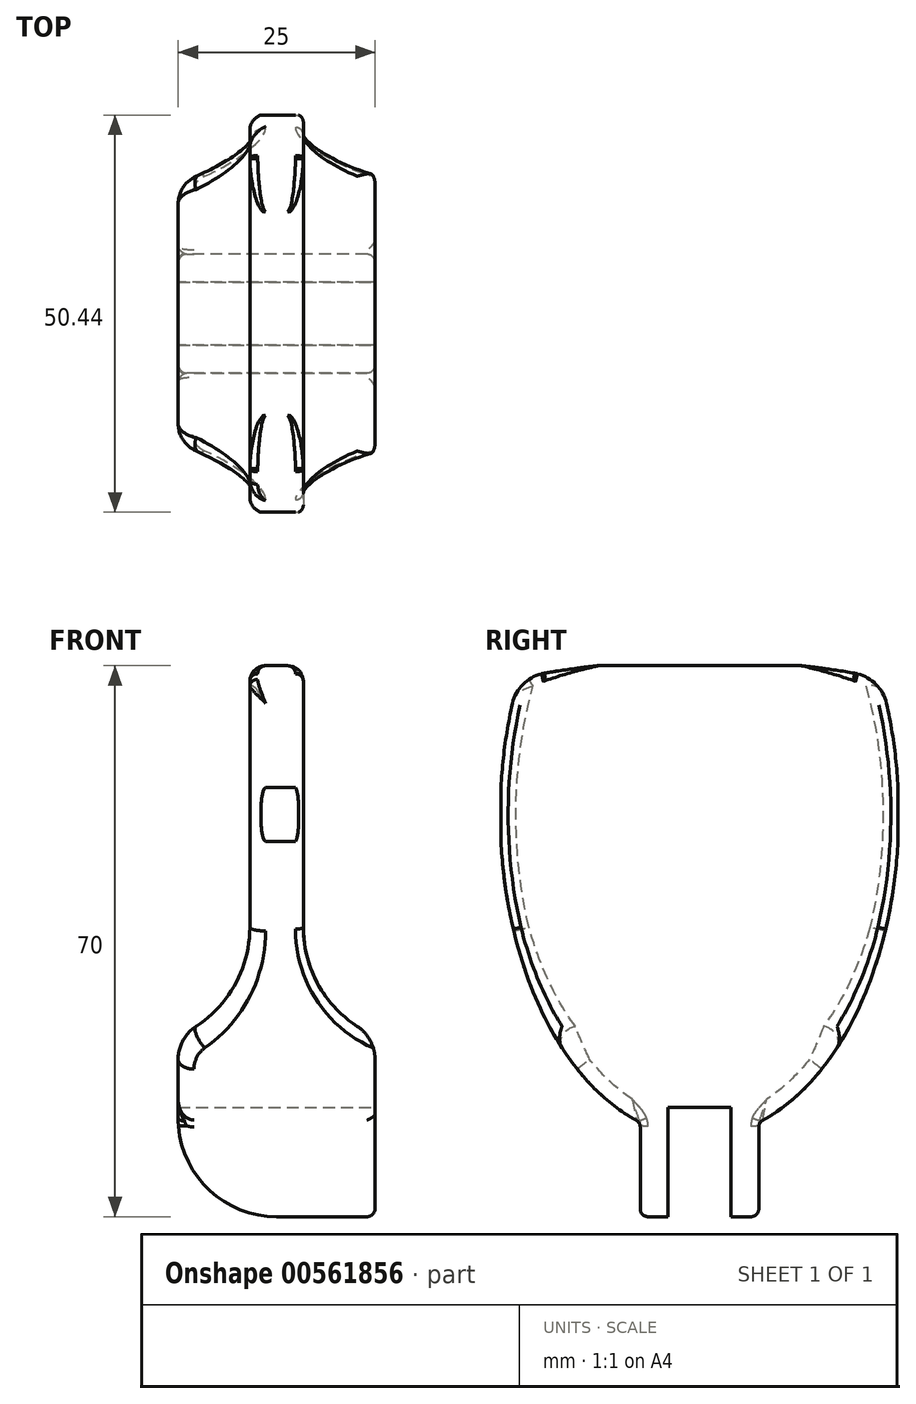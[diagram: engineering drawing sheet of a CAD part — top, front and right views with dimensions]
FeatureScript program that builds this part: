
annotation { "Feature Type Name" : "Feature", "Feature Type Description" : "" }
export const myFeature = defineFeature(function(context is Context, id is Id, definition is map)
    precondition{}
    {
        {
            var Q0;
            Q0=qCreatedBy(makeId("Front.planeOp"),FACE);
            var sketch = newSketch(context, id + "F0", { "sketchPlane" : qUnion([Q0])});
            skArc(sketch, "E0", {"start": v(-12.5, -14.27) * mm, "mid": v(-8.84, -23.11) * mm, "end": v(0, -26.77) * mm});
            skLineSegment(sketch, "E1.top", {"start": v(1.4, 43.23) * mm, "end": v(-1.4, 43.23) * mm});
            skLineSegment(sketch, "E1.left", {"start": v(3.4, 10) * mm, "end": v(3.4, 41.23) * mm});
            skLineSegment(sketch, "E1.right", {"start": v(-3.4, 10) * mm, "end": v(-3.4, 41.23) * mm});
            skPoint(sketch, "E1.middle", {"position": v(0, 20.49) * mm});
            skLineSegment(sketch, "E2.bottom", {"start": v(-7.5, -1.77) * mm, "end": v(7.5, -1.77) * mm});
            skLineSegment(sketch, "E2.top", {"start": v(0, -26.77) * mm, "end": v(11.5, -26.77) * mm});
            skLineSegment(sketch, "E2.left", {"start": v(-12.5, -6.77) * mm, "end": v(-12.5, -14.27) * mm});
            skLineSegment(sketch, "E2.right", {"start": v(12.5, -6.77) * mm, "end": v(12.5, -25.77) * mm});
            skArc(sketch, "E3", {"start": v(-7.5, -1.77) * mm, "mid": v(-11.04, -3.24) * mm, "end": v(-12.5, -6.77) * mm});
            skArc(sketch, "E4", {"start": v(12.5, -6.77) * mm, "mid": v(11.04, -3.24) * mm, "end": v(7.5, -1.77) * mm});
            skArc(sketch, "E5", {"start": v(-10.22, -2.58) * mm, "mid": v(-5.22, 2.84) * mm, "end": v(-3.4, 10) * mm});
            skArc(sketch, "E6", {"start": v(3.4, 10) * mm, "mid": v(5.22, 2.84) * mm, "end": v(10.22, -2.58) * mm});
            skPoint(sketch, "E7.orphan", {"position": v(-3.4, -2.25) * mm});
            skPoint(sketch, "E8.trimOffspring.end.orphan", {"position": v(3.4, -2.25) * mm});
            skArc(sketch, "E9", {"start": v(11.5, -26.77) * mm, "mid": v(12.2, -26.48) * mm, "end": v(12.5, -25.77) * mm});
            skPoint(sketch, "E10.visualSharp", {"position": v(-3.4, 43.23) * mm});
            skArc(sketch, "E10.filletArc", {"start": v(-1.4, 43.23) * mm, "mid": v(-2.81, 42.64) * mm, "end": v(-3.4, 41.23) * mm});
            skPoint(sketch, "E11.visualSharp", {"position": v(3.4, 43.23) * mm});
            skArc(sketch, "E11.filletArc", {"start": v(3.4, 41.23) * mm, "mid": v(2.81, 42.64) * mm, "end": v(1.4, 43.23) * mm});
            skSolve(sketch);
        }
        {
            var Q0;
            Q0=makeQuery(id+"F0.imprint","IMPRINT",FACE,{"disambiguationData":[TD([[makeQuery(id+"F0.imprint","IMPRINT",EDGE,{"derivedFrom":sQuery(id+"F0.wireOp",EDGE,"E1.top")}),1.0]])]});
            var Q1;
            Q1=makeQuery(id+"F0.imprint","IMPRINT",FACE,{"disambiguationData":[TD([[makeQuery(id+"F0.imprint","IMPRINT",EDGE,{"derivedFrom":sQuery(id+"F0.wireOp",EDGE,"E0")}),1.0]])]});
            extrude(context, id + "F1", {"entities" : qUnion([Q0, Q1]), "endBound" : BoundingType.SYMMETRIC, "depth" : 50.43 * mm, "offsetDistance" : 25 * mm});
        }
        {
            var Q0;
            Q0=makeQuery(id+"F1.opExtrude","SWEPT_FACE",FACE,{"disambiguationData":[OSD([sQuery(id+"F0.wireOp",EDGE,"E2.right")])]});
            cPlane(context, id + "F2", {"entities" : qUnion([Q0]), "cplaneType" : CPlaneType.OFFSET, "offset" : 0 * mm, "width" : 150 * mm, "height" : 150 * mm});
        }
        {
            var Q0;
            Q0=qCreatedBy(id+"F2.planeOp",FACE);
            var sketch = newSketch(context, id + "F3", { "sketchPlane" : qUnion([Q0])});
            skLineSegment(sketch, "E12.bottom", {"start": v(-26.66, 43.94) * mm, "end": v(27.44, 43.94) * mm});
            skLineSegment(sketch, "E12.top", {"start": v(-26.66, -27.37) * mm, "end": v(27.44, -27.37) * mm});
            skLineSegment(sketch, "E12.left", {"start": v(-26.66, 43.94) * mm, "end": v(-26.66, -27.37) * mm});
            skLineSegment(sketch, "E12.right", {"start": v(27.44, 43.94) * mm, "end": v(27.44, -27.37) * mm});
            skLineSegment(sketch, "E13.bottom", {"start": v(4, -26.88) * mm, "end": v(-4, -26.88) * mm});
            skLineSegment(sketch, "E13.top", {"start": v(4, -12.88) * mm, "end": v(-4, -12.88) * mm});
            skLineSegment(sketch, "E13.left", {"start": v(4, -26.88) * mm, "end": v(4, -12.88) * mm});
            skLineSegment(sketch, "E13.right", {"start": v(-4, -26.88) * mm, "end": v(-4, -12.88) * mm});
            skPoint(sketch, "E13.middle", {"position": v(0, -19.88) * mm});
            skLineSegment(sketch, "E14.top", {"start": v(7.5, -26.88) * mm, "end": v(-7.5, -26.88) * mm});
            skPoint(sketch, "E14.middle", {"position": v(0, -18.2) * mm});
            skLineSegment(sketch, "E15.bottom", {"start": v(7.53, -26.88) * mm, "end": v(27.44, -26.88) * mm});
            skLineSegment(sketch, "E15.top", {"start": v(7.53, -12.88) * mm, "end": v(27.44, -12.88) * mm});
            skLineSegment(sketch, "E15.left", {"start": v(7.53, -26.88) * mm, "end": v(7.53, -12.88) * mm});
            skLineSegment(sketch, "E15.right", {"start": v(27.44, -26.88) * mm, "end": v(27.44, -12.88) * mm});
            skLineSegment(sketch, "E16.bottom", {"start": v(-7.53, -26.88) * mm, "end": v(-26.66, -26.88) * mm});
            skLineSegment(sketch, "E16.top", {"start": v(-7.53, -12.88) * mm, "end": v(-26.66, -12.88) * mm});
            skLineSegment(sketch, "E16.left", {"start": v(-7.53, -26.88) * mm, "end": v(-7.53, -12.88) * mm});
            skLineSegment(sketch, "E16.right", {"start": v(-26.66, -26.88) * mm, "end": v(-26.66, -12.88) * mm});
            skArc(sketch, "E17", {"start": v(19.71, 42.27) * mm, "mid": v(0, 43.94) * mm, "end": v(-19.71, 42.27) * mm});
            skArc(sketch, "E18", {"start": v(-17.38, 13.5) * mm, "mid": v(0, -0.88) * mm, "end": v(17.38, 13.5) * mm});
            skEllipticalArc(sketch, "E19", {});
            skFitSpline(sketch, "E20.0", {"points": [v(1.4, 58.28) * mm, v(0, 58.39) * mm, v(-1.4, 58.28) * mm, v(-2.82, 57.94) * mm, v(-4.3, 57.34) * mm, v(-5.83, 56.46) * mm, v(-7.4, 55.26) * mm, v(-8.97, 53.74) * mm, v(-10.27, 52.2) * mm, v(-11.28, 50.79) * mm, v(-12.02, 49.65) * mm, v(-12.73, 48.43) * mm, v(-13.64, 46.73) * mm, v(-14.7, 44.44) * mm, v(-15.8, 41.46) * mm, v(-16.72, 38.3) * mm, v(-17.45, 34.97) * mm, v(-18, 31.5) * mm, v(-18.27, 28.54) * mm, v(-18.38, 26.14) * mm, v(-18.4, 24.31) * mm, v(-18.38, 22.5) * mm, v(-18.27, 20.09) * mm, v(-18, 17.12) * mm, v(-17.45, 13.66) * mm, v(-16.72, 10.33) * mm, v(-15.8, 7.16) * mm, v(-14.7, 4.2) * mm, v(-13.64, 1.9) * mm, v(-12.73, 0.2) * mm, v(-12.02, -1.02) * mm, v(-11.28, -2.16) * mm, v(-10.27, -3.57) * mm, v(-8.97, -5.11) * mm, v(-7.4, -6.64) * mm, v(-5.83, -7.83) * mm, v(-4.3, -8.71) * mm, v(-2.82, -9.3) * mm, v(-1.4, -9.65) * mm, v(0, -9.76) * mm, v(1.4, -9.65) * mm, v(2.82, -9.3) * mm, v(4.3, -8.71) * mm, v(5.83, -7.83) * mm, v(7.4, -6.64) * mm, v(8.97, -5.11) * mm, v(10.27, -3.57) * mm, v(11.28, -2.16) * mm, v(12.02, -1.02) * mm, v(12.73, 0.2) * mm, v(13.64, 1.9) * mm, v(14.7, 4.2) * mm, v(15.8, 7.16) * mm, v(16.72, 10.33) * mm, v(17.45, 13.66) * mm, v(18, 17.12) * mm, v(18.27, 20.09) * mm, v(18.38, 22.5) * mm, v(18.4, 24.31) * mm, v(18.38, 26.14) * mm, v(18.27, 28.54) * mm, v(18, 31.5) * mm, v(17.45, 34.97) * mm, v(16.72, 38.3) * mm, v(15.8, 41.46) * mm, v(14.7, 44.44) * mm, v(13.64, 46.73) * mm, v(12.73, 48.43) * mm, v(12.02, 49.65) * mm, v(11.28, 50.79) * mm, v(10.27, 52.2) * mm, v(8.97, 53.74) * mm, v(7.4, 55.26) * mm, v(5.83, 56.46) * mm, v(4.3, 57.34) * mm, v(2.82, 57.94) * mm, v(1.4, 58.28) * mm, v(0, 58.39) * mm, v(-1.4, 58.28) * mm]});
            skFitSpline(sketch, "E21.trimOffspring", {"points": [v(1.4, 58.28) * mm, v(0, 58.39) * mm, v(-1.4, 58.28) * mm, v(-2.82, 57.94) * mm, v(-4.3, 57.34) * mm, v(-5.83, 56.46) * mm, v(-7.4, 55.26) * mm, v(-8.97, 53.74) * mm, v(-10.27, 52.2) * mm, v(-11.28, 50.79) * mm, v(-12.02, 49.65) * mm, v(-12.73, 48.43) * mm, v(-13.64, 46.73) * mm, v(-14.7, 44.44) * mm, v(-15.8, 41.46) * mm, v(-16.72, 38.3) * mm, v(-17.45, 34.97) * mm, v(-18, 31.5) * mm, v(-18.27, 28.54) * mm, v(-18.38, 26.14) * mm, v(-18.4, 24.31) * mm, v(-18.38, 22.5) * mm, v(-18.27, 20.09) * mm, v(-18, 17.12) * mm, v(-17.45, 13.66) * mm, v(-16.72, 10.33) * mm, v(-15.8, 7.16) * mm, v(-14.7, 4.2) * mm, v(-13.64, 1.9) * mm, v(-12.73, 0.2) * mm, v(-12.02, -1.02) * mm, v(-11.28, -2.16) * mm, v(-10.27, -3.57) * mm, v(-8.97, -5.11) * mm, v(-7.4, -6.64) * mm, v(-5.83, -7.83) * mm, v(-4.3, -8.71) * mm, v(-2.82, -9.3) * mm, v(-1.4, -9.65) * mm, v(0, -9.76) * mm, v(1.4, -9.65) * mm, v(2.82, -9.3) * mm, v(4.3, -8.71) * mm, v(5.83, -7.83) * mm, v(7.4, -6.64) * mm, v(8.97, -5.11) * mm, v(10.27, -3.57) * mm, v(11.28, -2.16) * mm, v(12.02, -1.02) * mm, v(12.73, 0.2) * mm, v(13.64, 1.9) * mm, v(14.7, 4.2) * mm, v(15.8, 7.16) * mm, v(16.72, 10.33) * mm, v(17.45, 13.66) * mm, v(18, 17.12) * mm, v(18.27, 20.09) * mm, v(18.38, 22.5) * mm, v(18.4, 24.31) * mm, v(18.38, 26.14) * mm, v(18.27, 28.54) * mm, v(18, 31.5) * mm, v(17.45, 34.97) * mm, v(16.72, 38.3) * mm, v(15.8, 41.46) * mm, v(14.7, 44.44) * mm, v(13.64, 46.73) * mm, v(12.73, 48.43) * mm, v(12.02, 49.65) * mm, v(11.28, 50.79) * mm, v(10.27, 52.2) * mm, v(8.97, 53.74) * mm, v(7.4, 55.26) * mm, v(5.83, 56.46) * mm, v(4.3, 57.34) * mm, v(2.82, 57.94) * mm, v(1.4, 58.28) * mm, v(0, 58.39) * mm, v(-1.4, 58.28) * mm]});
            skEllipticalArc(sketch, "E22.trimOffspring", {});
            skArc(sketch, "E23.trimOffspring", {"start": v(17.28, 35.67) * mm, "mid": v(0, 37.03) * mm, "end": v(-17.28, 35.67) * mm});
            skPoint(sketch, "E24.visualSharp", {"position": v(-22.92, 41.68) * mm});
            skArc(sketch, "E24.filletArc", {"start": v(-19.71, 42.27) * mm, "mid": v(-22.31, 40.97) * mm, "end": v(-23.75, 38.45) * mm});
            skPoint(sketch, "E25.visualSharp", {"position": v(22.92, 41.68) * mm});
            skArc(sketch, "E25.filletArc", {"start": v(23.75, 38.45) * mm, "mid": v(22.31, 40.97) * mm, "end": v(19.71, 42.27) * mm});
            const initialGuessF3  = {"E19": [0, 0.02431378650389769, 0, 1, 0.040948620362707154, 0.02530453173425501, 1.218304167247893, 2.83944091341062], "E22.trimOffspring": [-3.4531458895558287e-09, 0.02431372548767801, -5.071851758616154e-07, 1, 0.04095312103342927, 0.02530426842214503, 3.443746959321061, 5.0648344110688175]};
            skSetInitialGuess(sketch, initialGuessF3);
            skSolve(sketch);
        }
        {
            var Q0;
            Q0=makeQuery(id+"F3.imprint","IMPRINT",FACE,{"disambiguationData":[TD([[makeQuery(id+"F3.imprint","IMPRINT",EDGE,{"derivedFrom":sQuery(id+"F3.wireOp",EDGE,"E13.top")}),1.0]])]});
            var Q1;
            Q1=makeQuery(id+"F3.imprint","IMPRINT",FACE,{"disambiguationData":[TD([[makeQuery(id+"F3.imprint","IMPRINT",EDGE,{"derivedFrom":sQuery(id+"F3.wireOp",EDGE,"E16.bottom")}),-1.0]])]});
            var Q2;
            Q2=makeQuery(id+"F3.imprint","IMPRINT",FACE,{"disambiguationData":[TD([[makeQuery(id+"F3.imprint","IMPRINT",EDGE,{"derivedFrom":sQuery(id+"F3.wireOp",EDGE,"E15.bottom")}),1.0]])]});
            var Q3;
            Q3=makeQuery(id+"F3.imprint","IMPRINT",FACE,{"disambiguationData":[TD([[makeQuery(id+"F3.imprint","IMPRINT",EDGE,{"derivedFrom":sQuery(id+"F3.wireOp",EDGE,"E18")}),1.0]])]});
            var Q4;
            {var subQ0=sQuery(id+"F3.wireOp",EDGE,"E25.filletArc");Q4=makeQuery(id+"F3.imprint","IMPRINT",FACE,{"disambiguationData":[TD([[makeQuery(id+"F3.imprint","IMPRINT",EDGE,{"derivedFrom":subQ0}),-1.0]])]});}
            var Q5;
            {var subQ0=sQuery(id+"F3.wireOp",EDGE,"E24.filletArc");Q5=makeQuery(id+"F3.imprint","IMPRINT",FACE,{"disambiguationData":[TD([[makeQuery(id+"F3.imprint","IMPRINT",EDGE,{"derivedFrom":subQ0}),-1.0]])]});}
            extrude(context, id + "F4", {"entities" : qUnion([Q0, Q1, Q2, Q3, Q4, Q5]), "operationType" : NewBodyOperationType.REMOVE, "oppositeDirection" : true, "depth" : 25 * mm, "offsetDistance" : 25 * mm});
        }
        {
            var Q0;
            Q0=makeQuery(id+"F4.boolean.opBoolean","INTERSECT",EDGE,{"derivedFrom":[makeQuery(id+"F1.opExtrude","SWEPT_FACE",FACE,{"disambiguationData":[OSD([sQuery(id+"F0.wireOp",EDGE,"E6")])]}),makeQuery(id+"F4.opExtrude","SWEPT_FACE",FACE,{"disambiguationData":[OSD([sQuery(id+"F3.wireOp",EDGE,"E18")])]})]});
            var Q1;
            Q1=makeQuery(id+"F4.boolean.opBoolean","INTERSECT",EDGE,{"derivedFrom":[makeQuery(id+"F1.opExtrude","SWEPT_FACE",FACE,{"disambiguationData":[OSD([sQuery(id+"F0.wireOp",EDGE,"E1.left")])]}),makeQuery(id+"F4.opExtrude","SWEPT_FACE",FACE,{"disambiguationData":[OSD([sQuery(id+"F3.wireOp",EDGE,"E20.0")])]})]});
            var Q2;
            Q2=makeQuery(id+"F4.boolean.opBoolean","INTERSECT",EDGE,{"derivedFrom":[makeQuery(id+"F1.opExtrude","SWEPT_FACE",FACE,{"disambiguationData":[OSD([sQuery(id+"F0.wireOp",EDGE,"E1.left")])]}),makeQuery(id+"F4.opExtrude","SWEPT_FACE",FACE,{"disambiguationData":[OSD([sQuery(id+"F3.wireOp",EDGE,"E23.trimOffspring")])]})]});
            var Q3;
            Q3=makeQuery(id+"F4.boolean.opBoolean","INTERSECT",EDGE,{"derivedFrom":[makeQuery(id+"F1.opExtrude","SWEPT_FACE",FACE,{"disambiguationData":[OSD([sQuery(id+"F0.wireOp",EDGE,"E1.left")])]}),makeQuery(id+"F4.opExtrude","SWEPT_FACE",FACE,{"disambiguationData":[OSD([sQuery(id+"F3.wireOp",EDGE,"E21.trimOffspring")])]})]});
            var Q4;
            Q4=makeQuery(id+"F4.boolean.opBoolean","INTERSECT",EDGE,{"derivedFrom":[makeQuery(id+"F1.opExtrude","SWEPT_FACE",FACE,{"disambiguationData":[OSD([sQuery(id+"F0.wireOp",EDGE,"E5")])]}),makeQuery(id+"F4.opExtrude","SWEPT_FACE",FACE,{"disambiguationData":[OSD([sQuery(id+"F3.wireOp",EDGE,"E19")])]})]});
            var Q5;
            Q5=makeQuery(id+"F4.boolean.opBoolean","INTERSECT",EDGE,{"derivedFrom":[makeQuery(id+"F1.opExtrude","SWEPT_FACE",FACE,{"disambiguationData":[OSD([sQuery(id+"F0.wireOp",EDGE,"E5")])]}),makeQuery(id+"F4.opExtrude","SWEPT_FACE",FACE,{"disambiguationData":[OSD([sQuery(id+"F3.wireOp",EDGE,"E22.trimOffspring")])]})]});
            var Q6;
            Q6=makeQuery(id+"F4.boolean.opBoolean","COPY",EDGE,{"derivedFrom":makeQuery(id+"F4.opExtrude","CAP_EDGE",EDGE,{"disambiguationData":[OSD([sQuery(id+"F3.wireOp",EDGE,"E22.trimOffspring")])],"isStart":true})});
            var Q7;
            Q7=makeQuery(id+"F4.boolean.opBoolean","COPY",EDGE,{"derivedFrom":makeQuery(id+"F4.opExtrude","CAP_EDGE",EDGE,{"disambiguationData":[OSD([sQuery(id+"F3.wireOp",EDGE,"E19")])],"isStart":true})});
            var Q8;
            Q8=makeQuery(id+"F4.boolean.opBoolean","INTERSECT",EDGE,{"derivedFrom":[makeQuery(id+"F1.opExtrude","SWEPT_FACE",FACE,{"disambiguationData":[OSD([sQuery(id+"F0.wireOp",EDGE,"E5")])]}),makeQuery(id+"F4.opExtrude","SWEPT_FACE",FACE,{"disambiguationData":[OSD([sQuery(id+"F3.wireOp",EDGE,"E18")])]})]});
            var Q9;
            Q9=makeQuery(id+"F4.boolean.opBoolean","INTERSECT",EDGE,{"derivedFrom":[makeQuery(id+"F1.opExtrude","SWEPT_FACE",FACE,{"disambiguationData":[OSD([sQuery(id+"F0.wireOp",EDGE,"E1.right")])]}),makeQuery(id+"F4.opExtrude","SWEPT_FACE",FACE,{"disambiguationData":[OSD([sQuery(id+"F3.wireOp",EDGE,"E20.0")])]})]});
            var Q10;
            Q10=makeQuery(id+"F4.boolean.opBoolean","INTERSECT",EDGE,{"derivedFrom":[makeQuery(id+"F1.opExtrude","SWEPT_FACE",FACE,{"disambiguationData":[OSD([sQuery(id+"F0.wireOp",EDGE,"E1.right")])]}),makeQuery(id+"F4.opExtrude","SWEPT_FACE",FACE,{"disambiguationData":[OSD([sQuery(id+"F3.wireOp",EDGE,"E23.trimOffspring")])]})]});
            var Q11;
            Q11=makeQuery(id+"F4.boolean.opBoolean","INTERSECT",EDGE,{"derivedFrom":[makeQuery(id+"F1.opExtrude","SWEPT_FACE",FACE,{"disambiguationData":[OSD([sQuery(id+"F0.wireOp",EDGE,"E1.right")])]}),makeQuery(id+"F4.opExtrude","SWEPT_FACE",FACE,{"disambiguationData":[OSD([sQuery(id+"F3.wireOp",EDGE,"E21.trimOffspring")])]})]});
            fillet(context, id + "F5", {"entities" : qUnion([Q0, Q1, Q2, Q3, Q4, Q5, Q6, Q7, Q8, Q9, Q10, Q11]), "radius" : 2 * mm, "tangentPropagation" : true, "allowEdgeOverflow" : false});
        }
        {
            var Q0;
            {var subQ0=sQuery(id+"F3.wireOp",EDGE,"E17");Q0=makeQuery(id+"F4.boolean.opBoolean","INTERSECT",EDGE,{"derivedFrom":[makeQuery(id+"F1.opExtrude","SWEPT_FACE",FACE,{"disambiguationData":[OSD([sQuery(id+"F0.wireOp",EDGE,"E11.filletArc")])]}),makeQuery(id+"F4.opExtrude","SWEPT_FACE",FACE,{"disambiguationData":[OSD([subQ0]),TDD([makeQuery(id+"F3.imprint","IMPRINT",EDGE,{"disambiguationData":[TD([[makeQuery(id+"F3.imprint","INTERSECT",VERTEX,{"derivedFrom":[subQ0,sQuery(id+"F3.wireOp",EDGE,"E24.filletArc")]}),1.0]])],"derivedFrom":subQ0})])]})]});}
            var Q1;
            Q1=makeQuery(id+"F5.opFillet","BLEND_EDGE",EDGE,{"blendedFrom":[makeQuery(id+"F4.boolean.opBoolean","INTERSECT",EDGE,{"disambiguationData":[OD(1.0)],"derivedFrom":[makeQuery(id+"F1.opExtrude","SWEPT_FACE",FACE,{"disambiguationData":[OSD([sQuery(id+"F0.wireOp",EDGE,"E1.left")])]}),makeQuery(id+"F4.opExtrude","SWEPT_FACE",FACE,{"disambiguationData":[OSD([sQuery(id+"F3.wireOp",EDGE,"E22.trimOffspring")])]})]}),makeQuery(id+"F4.boolean.opBoolean","COPY",FACE,{"derivedFrom":makeQuery(id+"F4.opExtrude","SWEPT_FACE",FACE,{"disambiguationData":[OSD([sQuery(id+"F3.wireOp",EDGE,"E25.filletArc")])]})})],"blendedInto":[makeQuery(id+"F4.boolean.opBoolean","COPY",FACE,{"derivedFrom":makeQuery(id+"F4.opExtrude","SWEPT_FACE",FACE,{"disambiguationData":[OSD([sQuery(id+"F3.wireOp",EDGE,"E25.filletArc")])]})})]});
            var Q2;
            {var subQ0=sQuery(id+"F3.wireOp",EDGE,"E17");Q2=makeQuery(id+"F4.boolean.opBoolean","INTERSECT",EDGE,{"derivedFrom":[makeQuery(id+"F1.opExtrude","SWEPT_FACE",FACE,{"disambiguationData":[OSD([sQuery(id+"F0.wireOp",EDGE,"E10.filletArc")])]}),makeQuery(id+"F4.opExtrude","SWEPT_FACE",FACE,{"disambiguationData":[OSD([subQ0]),TDD([makeQuery(id+"F3.imprint","IMPRINT",EDGE,{"disambiguationData":[TD([[makeQuery(id+"F3.imprint","INTERSECT",VERTEX,{"derivedFrom":[subQ0,sQuery(id+"F3.wireOp",EDGE,"E25.filletArc")]}),-1.0]])],"derivedFrom":subQ0})])]})]});}
            var Q3;
            Q3=makeQuery(id+"F5.opFillet","BLEND_EDGE",EDGE,{"blendedFrom":[makeQuery(id+"F4.boolean.opBoolean","INTERSECT",EDGE,{"disambiguationData":[OD(1.0)],"derivedFrom":[makeQuery(id+"F1.opExtrude","SWEPT_FACE",FACE,{"disambiguationData":[OSD([sQuery(id+"F0.wireOp",EDGE,"E1.left")])]}),makeQuery(id+"F4.opExtrude","SWEPT_FACE",FACE,{"disambiguationData":[OSD([sQuery(id+"F3.wireOp",EDGE,"E19")])]})]}),makeQuery(id+"F4.boolean.opBoolean","COPY",FACE,{"derivedFrom":makeQuery(id+"F4.opExtrude","SWEPT_FACE",FACE,{"disambiguationData":[OSD([sQuery(id+"F3.wireOp",EDGE,"E24.filletArc")])]})})],"blendedInto":[makeQuery(id+"F4.boolean.opBoolean","COPY",FACE,{"derivedFrom":makeQuery(id+"F4.opExtrude","SWEPT_FACE",FACE,{"disambiguationData":[OSD([sQuery(id+"F3.wireOp",EDGE,"E24.filletArc")])]})})]});
            var Q4;
            Q4=makeQuery(id+"F5.opFillet","BLEND_EDGE",EDGE,{"blendedFrom":[makeQuery(id+"F4.boolean.opBoolean","INTERSECT",EDGE,{"disambiguationData":[OD(1.0)],"derivedFrom":[makeQuery(id+"F1.opExtrude","SWEPT_FACE",FACE,{"disambiguationData":[OSD([sQuery(id+"F0.wireOp",EDGE,"E1.right")])]}),makeQuery(id+"F4.opExtrude","SWEPT_FACE",FACE,{"disambiguationData":[OSD([sQuery(id+"F3.wireOp",EDGE,"E19")])]})]}),makeQuery(id+"F4.boolean.opBoolean","COPY",FACE,{"derivedFrom":makeQuery(id+"F4.opExtrude","SWEPT_FACE",FACE,{"disambiguationData":[OSD([sQuery(id+"F3.wireOp",EDGE,"E24.filletArc")])]})})],"blendedInto":[makeQuery(id+"F4.boolean.opBoolean","COPY",FACE,{"derivedFrom":makeQuery(id+"F4.opExtrude","SWEPT_FACE",FACE,{"disambiguationData":[OSD([sQuery(id+"F3.wireOp",EDGE,"E24.filletArc")])]})})]});
            var Q5;
            Q5=makeQuery(id+"F4.boolean.opBoolean","COPY",EDGE,{"derivedFrom":makeQuery(id+"F4.opExtrude","CAP_EDGE",EDGE,{"disambiguationData":[OSD([sQuery(id+"F3.wireOp",EDGE,"E13.right")])],"isStart":true})});
            var Q6;
            Q6=makeQuery(id+"F4.boolean.opBoolean","COPY",EDGE,{"derivedFrom":makeQuery(id+"F4.opExtrude","CAP_EDGE",EDGE,{"disambiguationData":[OSD([sQuery(id+"F3.wireOp",EDGE,"E13.left")])],"isStart":true})});
            var Q7;
            Q7=makeQuery(id+"F4.boolean.opBoolean","COPY",EDGE,{"derivedFrom":makeQuery(id+"F4.opExtrude","CAP_EDGE",EDGE,{"disambiguationData":[OSD([sQuery(id+"F3.wireOp",EDGE,"E13.top")])],"isStart":true})});
            var Q8;
            Q8=makeQuery(id+"F4.boolean.opBoolean","INTERSECT",EDGE,{"derivedFrom":[makeQuery(id+"F1.opExtrude","SWEPT_FACE",FACE,{"disambiguationData":[OSD([sQuery(id+"F0.wireOp",EDGE,"E0")])]}),makeQuery(id+"F4.opExtrude","SWEPT_FACE",FACE,{"disambiguationData":[OSD([sQuery(id+"F3.wireOp",EDGE,"E16.left")])]})]});
            var Q9;
            Q9=makeQuery(id+"F4.boolean.opBoolean","INTERSECT",EDGE,{"derivedFrom":[makeQuery(id+"F1.opExtrude","SWEPT_FACE",FACE,{"disambiguationData":[OSD([sQuery(id+"F0.wireOp",EDGE,"E0")])]}),makeQuery(id+"F4.opExtrude","SWEPT_FACE",FACE,{"disambiguationData":[OSD([sQuery(id+"F3.wireOp",EDGE,"E15.left")])]})]});
            var Q10;
            Q10=makeQuery(id+"F4.boolean.opBoolean","COPY",EDGE,{"derivedFrom":makeQuery(id+"F4.opExtrude","SWEPT_EDGE",EDGE,{"disambiguationData":[OSD([sQuery(id+"F3.wireOp",EDGE,"E16.left"),sQuery(id+"F3.wireOp",EDGE,"E19")])]})});
            var Q11;
            Q11=makeQuery(id+"F4.boolean.opBoolean","COPY",EDGE,{"derivedFrom":makeQuery(id+"F4.opExtrude","SWEPT_EDGE",EDGE,{"disambiguationData":[OSD([sQuery(id+"F3.wireOp",EDGE,"E15.left"),sQuery(id+"F3.wireOp",EDGE,"E22.trimOffspring")])]})});
            fillet(context, id + "F6", {"entities" : qUnion([Q0, Q1, Q2, Q3, Q4, Q5, Q6, Q7, Q8, Q9, Q10, Q11]), "radius" : 1 * mm, "tangentPropagation" : true, "allowEdgeOverflow" : false});
        }
    });
